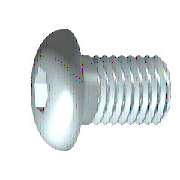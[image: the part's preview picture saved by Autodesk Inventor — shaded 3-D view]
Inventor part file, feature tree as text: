
AUTODESK INVENTOR PART (.ipt)
format: ipt  version: 2015 (Build 190159000, 159)  size: 203,264 bytes
history: native  units: mm (DEFAULTED — no unit token found)
features: sketch x2, other x1, extrude x1, plane x1
ambient origin geometry x7: Origin, YZ Plane, XY Plane, X Axis, Y Axis, Z Axis, Center Point
bodies: Body1 (feature_tree)
feature tree (5):
  other  "Bryła"
  extrude  "Szczelina"  Depth=8.0mm
  plane  "Work Plane1"
  sketch  "Szkic1"
  sketch  "Szkic2"
